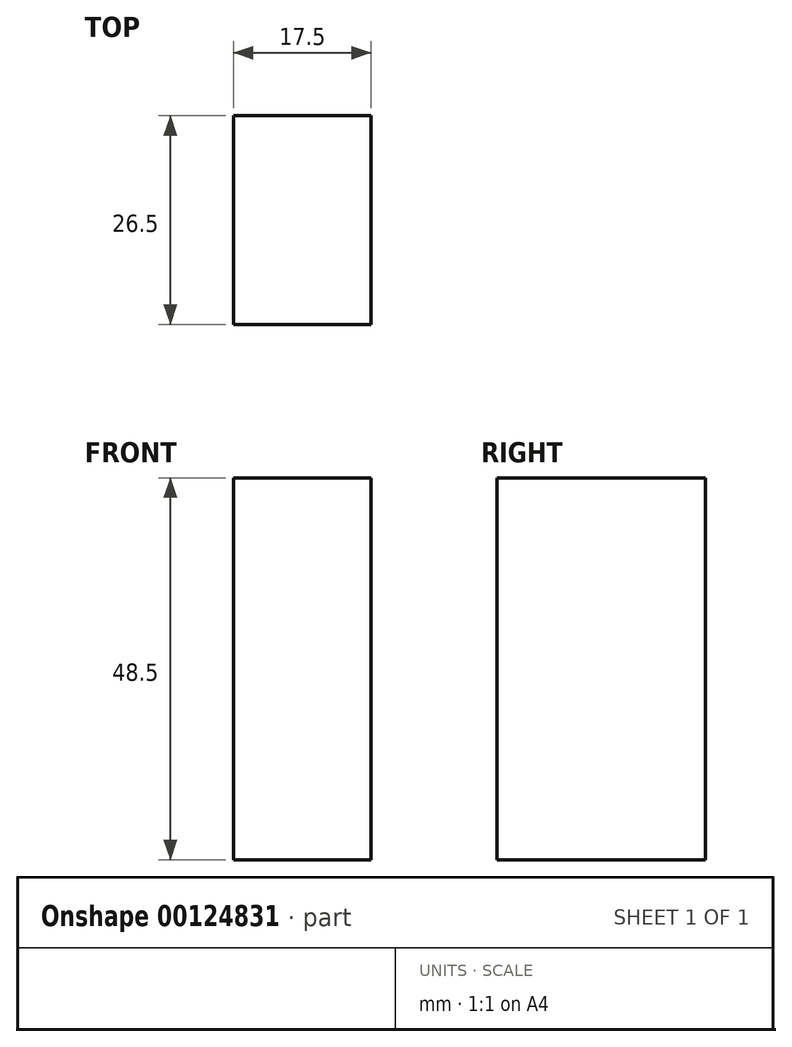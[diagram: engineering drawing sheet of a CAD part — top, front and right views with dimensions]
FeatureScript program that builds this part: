
annotation { "Feature Type Name" : "Feature", "Feature Type Description" : "" }
export const myFeature = defineFeature(function(context is Context, id is Id, definition is map)
    precondition{}
    {
        {
            var Q0;
            Q0=qCreatedBy(makeId("Right.planeOp"),FACE);
            var sketch = newSketch(context, id + "F0", { "sketchPlane" : qUnion([Q0])});
            skLineSegment(sketch, "E0.bottom", {"start": v(-29.72, 32.24) * mm, "end": v(-3.22, 32.24) * mm});
            skLineSegment(sketch, "E0.top", {"start": v(-29.72, -16.26) * mm, "end": v(-3.22, -16.26) * mm});
            skLineSegment(sketch, "E0.left", {"start": v(-29.72, 32.24) * mm, "end": v(-29.72, -16.26) * mm});
            skLineSegment(sketch, "E0.right", {"start": v(-3.22, 32.24) * mm, "end": v(-3.22, -16.26) * mm});
            skSolve(sketch);
        }
        {
            var Q0;
            Q0 = qSketchRegion(id + "F0", true);
            extrude(context, id + "F1", {"entities" : qUnion([Q0]), "depth" : 17.5 * mm});
        }
    });
